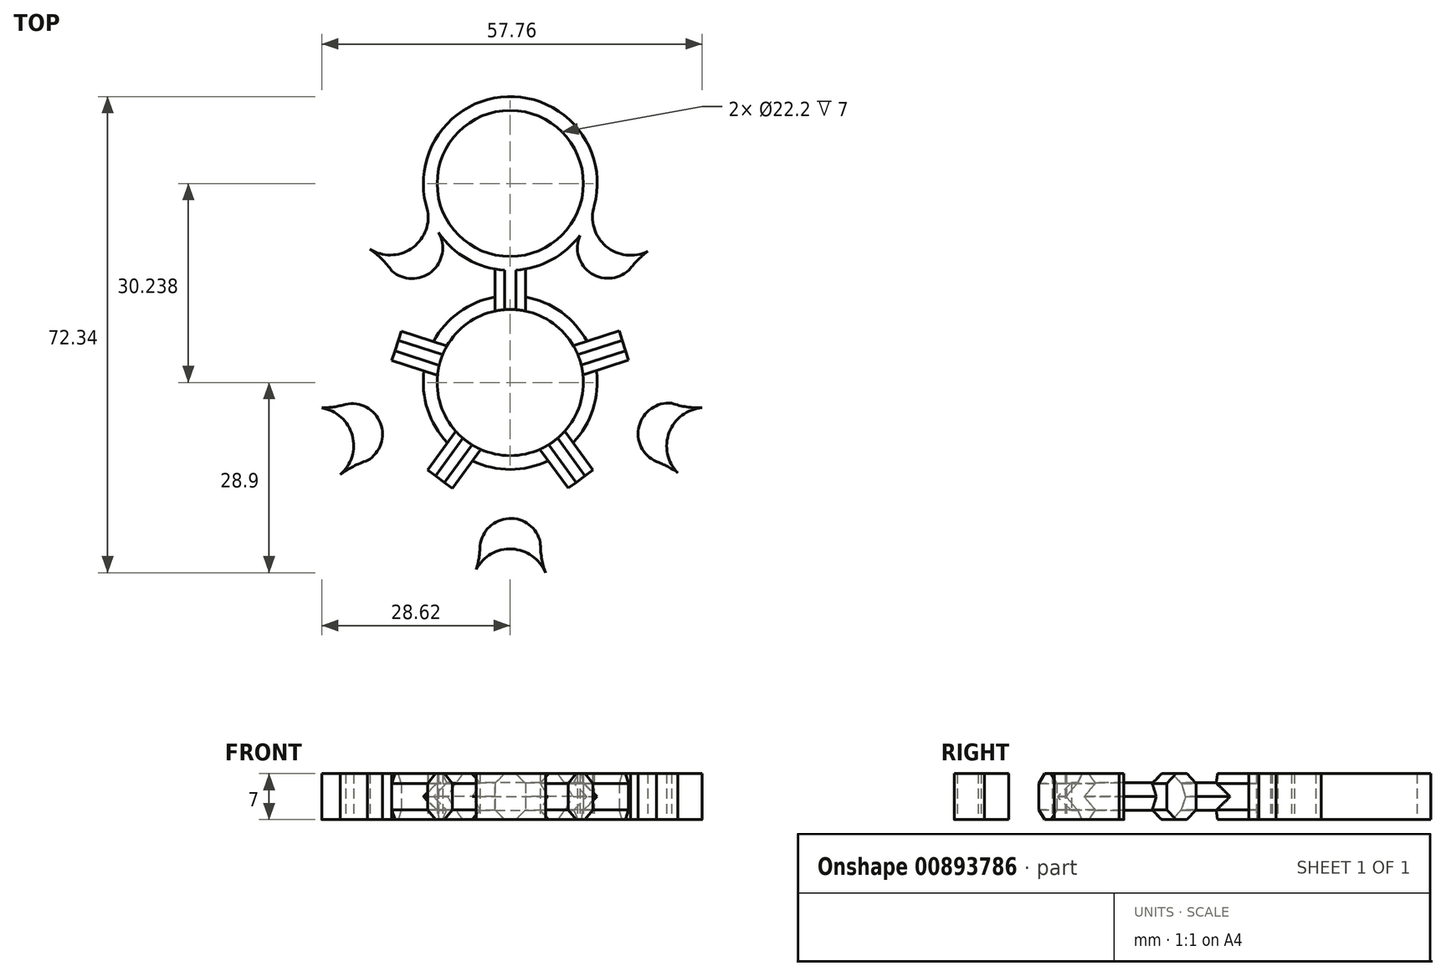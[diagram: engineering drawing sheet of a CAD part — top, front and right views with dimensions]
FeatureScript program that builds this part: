
annotation { "Feature Type Name" : "Feature", "Feature Type Description" : "" }
export const myFeature = defineFeature(function(context is Context, id is Id, definition is map)
    precondition{}
    {
        {
            var Q0;
            Q0=qCreatedBy(makeId("Top.planeOp"),FACE);
            var sketch = newSketch(context, id + "F0", { "sketchPlane" : qUnion([Q0])});
            skCircle(sketch, "E0", {"center": v(0, 0) * mm, "radius": 11.1 * mm});
            skCircle(sketch, "E1", {"center": v(0, 0) * mm, "radius": 13.2 * mm});
            skLineSegment(sketch, "E2", {"start": v(-2.34, 13) * mm, "end": v(-2.34, 18.14) * mm});
            skLineSegment(sketch, "E3", {"start": v(-2.34, 18.14) * mm, "end": v(2.33, 18.14) * mm});
            skLineSegment(sketch, "E4", {"start": v(2.33, 18.14) * mm, "end": v(2.33, 13) * mm});
            skCircle(sketch, "E5", {"center": v(0, 30.24) * mm, "radius": 13.2 * mm});
            skCircle(sketch, "E6", {"center": v(0, 30.24) * mm, "radius": 11.1 * mm});
            skCircle(sketch, "E7.1.0", {"center": v(-28.76, 9.34) * mm, "radius": 13.2 * mm});
            skCircle(sketch, "E7.1.1", {"center": v(-28.76, 9.34) * mm, "radius": 11.1 * mm});
            skLineSegment(sketch, "E7.1.2", {"start": v(-16.53, 7.82) * mm, "end": v(-11.64, 6.23) * mm});
            skLineSegment(sketch, "E7.1.3", {"start": v(-13.08, 1.78) * mm, "end": v(-17.98, 3.38) * mm});
            skLineSegment(sketch, "E7.1.4", {"start": v(-17.98, 3.38) * mm, "end": v(-16.53, 7.82) * mm});
            skCircle(sketch, "E7.2.0", {"center": v(-17.77, -24.46) * mm, "radius": 13.2 * mm});
            skCircle(sketch, "E7.2.1", {"center": v(-17.77, -24.46) * mm, "radius": 11.1 * mm});
            skLineSegment(sketch, "E7.2.2", {"start": v(-12.55, -13.3) * mm, "end": v(-9.52, -9.14) * mm});
            skLineSegment(sketch, "E7.2.3", {"start": v(-5.74, -11.89) * mm, "end": v(-8.77, -16.05) * mm});
            skLineSegment(sketch, "E7.2.4", {"start": v(-8.77, -16.05) * mm, "end": v(-12.55, -13.3) * mm});
            skCircle(sketch, "E7.3.0", {"center": v(17.77, -24.46) * mm, "radius": 13.2 * mm});
            skCircle(sketch, "E7.3.1", {"center": v(17.77, -24.46) * mm, "radius": 11.1 * mm});
            skLineSegment(sketch, "E7.3.2", {"start": v(8.78, -16.05) * mm, "end": v(5.75, -11.88) * mm});
            skLineSegment(sketch, "E7.3.3", {"start": v(9.53, -9.13) * mm, "end": v(12.56, -13.3) * mm});
            skLineSegment(sketch, "E7.3.4", {"start": v(12.56, -13.3) * mm, "end": v(8.78, -16.05) * mm});
            skCircle(sketch, "E7.4.0", {"center": v(28.76, 9.34) * mm, "radius": 13.2 * mm});
            skCircle(sketch, "E7.4.1", {"center": v(28.76, 9.34) * mm, "radius": 11.1 * mm});
            skLineSegment(sketch, "E7.4.2", {"start": v(17.97, 3.39) * mm, "end": v(13.08, 1.8) * mm});
            skLineSegment(sketch, "E7.4.3", {"start": v(11.63, 6.24) * mm, "end": v(16.53, 7.83) * mm});
            skLineSegment(sketch, "E7.4.4", {"start": v(16.53, 7.83) * mm, "end": v(17.97, 3.39) * mm});
            skArc(sketch, "E8", {"start": v(-17.98, 16.96) * mm, "mid": v(-11.96, 16.83) * mm, "end": v(-10.87, 22.75) * mm});
            skArc(sketch, "E9", {"start": v(-21.6, 20.43) * mm, "mid": v(-15.2, 20.23) * mm, "end": v(-12.5, 26.02) * mm});
            skArc(sketch, "E10.1.0", {"start": v(-26.1, -14.22) * mm, "mid": v(-23.93, -8.2) * mm, "end": v(-28.62, -3.86) * mm});
            skArc(sketch, "E10.1.1", {"start": v(-21.68, -11.86) * mm, "mid": v(-19.7, -6.17) * mm, "end": v(-25, -3.3) * mm});
            skArc(sketch, "E10.2.0", {"start": v(5.46, -29.22) * mm, "mid": v(0.41, -25.3) * mm, "end": v(-5.18, -28.4) * mm});
            skArc(sketch, "E10.2.1", {"start": v(4.57, -24.29) * mm, "mid": v(-0.22, -20.65) * mm, "end": v(-4.58, -24.8) * mm});
            skArc(sketch, "E10.3.0", {"start": v(29.48, -3.84) * mm, "mid": v(24.19, -7.43) * mm, "end": v(25.42, -13.7) * mm});
            skArc(sketch, "E10.3.1", {"start": v(24.51, -3.15) * mm, "mid": v(19.57, -6.59) * mm, "end": v(22.17, -12.02) * mm});
            skArc(sketch, "E10.4.0", {"start": v(12.76, 26.85) * mm, "mid": v(14.54, 20.7) * mm, "end": v(20.88, 19.94) * mm});
            skArc(sketch, "E10.4.1", {"start": v(10.57, 22.34) * mm, "mid": v(12.31, 16.58) * mm, "end": v(18.28, 17.37) * mm});
            skSolve(sketch);
        }
        {
            var Q0;
            {var subQ0=sQuery(id+"F0.wireOp",EDGE,"E8");Q0=makeQuery(id+"F0.imprint","IMPRINT",FACE,{"disambiguationData":[TD([[makeQuery(id+"F0.imprint","IMPRINT",EDGE,{"derivedFrom":subQ0}),1.0]])]});}
            var Q1;
            Q1=makeQuery(id+"F0.imprint","IMPRINT",FACE,{"disambiguationData":[TD([[makeQuery(id+"F0.imprint","IMPRINT",EDGE,{"derivedFrom":sQuery(id+"F0.wireOp",EDGE,"E7.1.1")}),-1.0]])]});
            var Q2;
            {var subQ5=sQuery(id+"F0.wireOp",EDGE,"E7.1.4");Q2=makeQuery(id+"F0.imprint","IMPRINT",FACE,{"disambiguationData":[TD([[makeQuery(id+"F0.imprint","IMPRINT",EDGE,{"derivedFrom":subQ5}),-1.0]])]});}
            var Q3;
            {var subQ0=sQuery(id+"F0.wireOp",EDGE,"E7.1.2");var subQ1=sQuery(id+"F0.wireOp",EDGE,"E1");var subQ2=makeQuery(id+"F0.imprint","INTERSECT",VERTEX,{"derivedFrom":[subQ1,subQ0]});Q3=makeQuery(id+"F0.imprint","IMPRINT",FACE,{"disambiguationData":[TD([[makeQuery(id+"F0.imprint","IMPRINT",EDGE,{"disambiguationData":[TD([[subQ2,-1.0]])],"derivedFrom":subQ1}),-1.0]])]});}
            var Q4;
            {var subQ0=sQuery(id+"F0.wireOp",EDGE,"E3");Q4=makeQuery(id+"F0.imprint","IMPRINT",FACE,{"disambiguationData":[TD([[makeQuery(id+"F0.imprint","IMPRINT",EDGE,{"derivedFrom":subQ0}),-1.0]])]});}
            var Q5;
            {var subQ4=sQuery(id+"F0.wireOp",EDGE,"E3");Q5=makeQuery(id+"F0.imprint","IMPRINT",FACE,{"disambiguationData":[TD([[makeQuery(id+"F0.imprint","IMPRINT",EDGE,{"derivedFrom":subQ4}),1.0]])]});}
            var Q6;
            {var subQ0=sQuery(id+"F0.wireOp",EDGE,"E10.4.1");Q6=makeQuery(id+"F0.imprint","IMPRINT",FACE,{"disambiguationData":[TD([[makeQuery(id+"F0.imprint","IMPRINT",EDGE,{"derivedFrom":subQ0}),1.0]])]});}
            var Q7;
            {var subQ5=sQuery(id+"F0.wireOp",EDGE,"E7.4.4");Q7=makeQuery(id+"F0.imprint","IMPRINT",FACE,{"disambiguationData":[TD([[makeQuery(id+"F0.imprint","IMPRINT",EDGE,{"derivedFrom":subQ5}),-1.0]])]});}
            var Q8;
            {var subQ5=sQuery(id+"F0.wireOp",EDGE,"E7.3.4");Q8=makeQuery(id+"F0.imprint","IMPRINT",FACE,{"disambiguationData":[TD([[makeQuery(id+"F0.imprint","IMPRINT",EDGE,{"derivedFrom":subQ5}),-1.0]])]});}
            var Q9;
            {var subQ5=sQuery(id+"F0.wireOp",EDGE,"E7.2.4");Q9=makeQuery(id+"F0.imprint","IMPRINT",FACE,{"disambiguationData":[TD([[makeQuery(id+"F0.imprint","IMPRINT",EDGE,{"derivedFrom":subQ5}),-1.0]])]});}
            var Q10;
            {var subQ0=sQuery(id+"F0.wireOp",EDGE,"E7.2.2");var subQ1=sQuery(id+"F0.wireOp",EDGE,"E1");var subQ2=makeQuery(id+"F0.imprint","INTERSECT",VERTEX,{"derivedFrom":[subQ1,subQ0]});Q10=makeQuery(id+"F0.imprint","IMPRINT",FACE,{"disambiguationData":[TD([[makeQuery(id+"F0.imprint","IMPRINT",EDGE,{"disambiguationData":[TD([[subQ2,-1.0]])],"derivedFrom":subQ1}),-1.0]])]});}
            var Q11;
            Q11=makeQuery(id+"F0.imprint","IMPRINT",FACE,{"disambiguationData":[TD([[makeQuery(id+"F0.imprint","IMPRINT",EDGE,{"derivedFrom":sQuery(id+"F0.wireOp",EDGE,"E0")}),-1.0]])]});
            var Q12;
            {var subQ0=sQuery(id+"F0.wireOp",EDGE,"E7.4.2");var subQ1=sQuery(id+"F0.wireOp",EDGE,"E1");var subQ2=makeQuery(id+"F0.imprint","INTERSECT",VERTEX,{"derivedFrom":[subQ1,subQ0]});Q12=makeQuery(id+"F0.imprint","IMPRINT",FACE,{"disambiguationData":[TD([[makeQuery(id+"F0.imprint","IMPRINT",EDGE,{"disambiguationData":[TD([[subQ2,-1.0]])],"derivedFrom":subQ1}),-1.0]])]});}
            var Q13;
            {var subQ0=sQuery(id+"F0.wireOp",EDGE,"E2");var subQ1=sQuery(id+"F0.wireOp",EDGE,"E1");var subQ2=makeQuery(id+"F0.imprint","INTERSECT",VERTEX,{"derivedFrom":[subQ1,subQ0]});Q13=makeQuery(id+"F0.imprint","IMPRINT",FACE,{"disambiguationData":[TD([[makeQuery(id+"F0.imprint","IMPRINT",EDGE,{"disambiguationData":[TD([[subQ2,1.0]])],"derivedFrom":subQ1}),-1.0]])]});}
            var Q14;
            {var subQ0=sQuery(id+"F0.wireOp",EDGE,"E7.3.2");var subQ1=sQuery(id+"F0.wireOp",EDGE,"E1");var subQ2=makeQuery(id+"F0.imprint","INTERSECT",VERTEX,{"derivedFrom":[subQ1,subQ0]});Q14=makeQuery(id+"F0.imprint","IMPRINT",FACE,{"disambiguationData":[TD([[makeQuery(id+"F0.imprint","IMPRINT",EDGE,{"disambiguationData":[TD([[subQ2,-1.0]])],"derivedFrom":subQ1}),-1.0]])]});}
            var Q15;
            Q15=makeQuery(id+"F0.imprint","IMPRINT",FACE,{"disambiguationData":[TD([[makeQuery(id+"F0.imprint","IMPRINT",EDGE,{"derivedFrom":sQuery(id+"F0.wireOp",EDGE,"E7.3.1")}),-1.0]])]});
            var Q16;
            {var subQ3=sQuery(id+"F0.wireOp",EDGE,"E10.2.1");Q16=makeQuery(id+"F0.imprint","IMPRINT",FACE,{"disambiguationData":[TD([[makeQuery(id+"F0.imprint","IMPRINT",EDGE,{"derivedFrom":subQ3}),1.0]])]});}
            var Q17;
            Q17=makeQuery(id+"F0.imprint","IMPRINT",FACE,{"disambiguationData":[TD([[makeQuery(id+"F0.imprint","IMPRINT",EDGE,{"derivedFrom":sQuery(id+"F0.wireOp",EDGE,"E7.2.1")}),-1.0]])]});
            var Q18;
            {var subQ3=sQuery(id+"F0.wireOp",EDGE,"E10.1.1");Q18=makeQuery(id+"F0.imprint","IMPRINT",FACE,{"disambiguationData":[TD([[makeQuery(id+"F0.imprint","IMPRINT",EDGE,{"derivedFrom":subQ3}),1.0]])]});}
            var Q19;
            Q19=makeQuery(id+"F0.imprint","IMPRINT",FACE,{"disambiguationData":[TD([[makeQuery(id+"F0.imprint","IMPRINT",EDGE,{"derivedFrom":sQuery(id+"F0.wireOp",EDGE,"E7.4.1")}),-1.0]])]});
            var Q20;
            {var subQ3=sQuery(id+"F0.wireOp",EDGE,"E10.3.1");Q20=makeQuery(id+"F0.imprint","IMPRINT",FACE,{"disambiguationData":[TD([[makeQuery(id+"F0.imprint","IMPRINT",EDGE,{"derivedFrom":subQ3}),1.0]])]});}
            extrude(context, id + "F1", {"entities" : qUnion([Q0, Q1, Q2, Q3, Q4, Q5, Q6, Q7, Q8, Q9, Q10, Q11, Q12, Q13, Q14, Q15, Q16, Q17, Q18, Q19, Q20]), "depth" : 7 * mm, "offsetDistance" : 25 * mm});
        }
        {
            var Q0;
            {var subQ0=sQuery(id+"F0.wireOp",EDGE,"E1");Q0=makeQuery(id+"F1.opExtrude","CAP_EDGE",EDGE,{"disambiguationData":[OSD([subQ0]),TDD([makeQuery(id+"F0.imprint","IMPRINT",EDGE,{"disambiguationData":[TD([[makeQuery(id+"F0.imprint","INTERSECT",VERTEX,{"derivedFrom":[subQ0,sQuery(id+"F0.wireOp",EDGE,"E7.3.3")]}),-1.0]])],"derivedFrom":subQ0})])],"isStart":false});}
            var Q1;
            {var subQ0=sQuery(id+"F0.wireOp",EDGE,"E1");Q1=makeQuery(id+"F1.opExtrude","CAP_EDGE",EDGE,{"disambiguationData":[OSD([subQ0]),TDD([makeQuery(id+"F0.imprint","IMPRINT",EDGE,{"disambiguationData":[TD([[makeQuery(id+"F0.imprint","INTERSECT",VERTEX,{"derivedFrom":[subQ0,sQuery(id+"F0.wireOp",EDGE,"E4")]}),1.0]])],"derivedFrom":subQ0})])],"isStart":false});}
            var Q2;
            {var subQ0=sQuery(id+"F0.wireOp",EDGE,"E1");Q2=makeQuery(id+"F1.opExtrude","CAP_EDGE",EDGE,{"disambiguationData":[OSD([subQ0]),TDD([makeQuery(id+"F0.imprint","IMPRINT",EDGE,{"disambiguationData":[TD([[makeQuery(id+"F0.imprint","INTERSECT",VERTEX,{"derivedFrom":[subQ0,sQuery(id+"F0.wireOp",EDGE,"E2")]}),-1.0]])],"derivedFrom":subQ0})])],"isStart":false});}
            var Q3;
            {var subQ0=sQuery(id+"F0.wireOp",EDGE,"E1");Q3=makeQuery(id+"F1.opExtrude","CAP_EDGE",EDGE,{"disambiguationData":[OSD([subQ0]),TDD([makeQuery(id+"F0.imprint","IMPRINT",EDGE,{"disambiguationData":[TD([[makeQuery(id+"F0.imprint","INTERSECT",VERTEX,{"derivedFrom":[subQ0,sQuery(id+"F0.wireOp",EDGE,"E7.1.3")]}),-1.0]])],"derivedFrom":subQ0})])],"isStart":false});}
            var Q4;
            {var subQ0=sQuery(id+"F0.wireOp",EDGE,"E1");Q4=makeQuery(id+"F1.opExtrude","CAP_EDGE",EDGE,{"disambiguationData":[OSD([subQ0]),TDD([makeQuery(id+"F0.imprint","IMPRINT",EDGE,{"disambiguationData":[TD([[makeQuery(id+"F0.imprint","INTERSECT",VERTEX,{"derivedFrom":[subQ0,sQuery(id+"F0.wireOp",EDGE,"E7.2.3")]}),-1.0]])],"derivedFrom":subQ0})])],"isStart":false});}
            chamfer(context, id + "F2", {"entities" : qUnion([Q0, Q1, Q2, Q3, Q4]), "width" : 3.5 * mm, "tangentPropagation" : true});
        }
        {
            var Q0;
            {var subQ0=sQuery(id+"F0.wireOp",EDGE,"E1");Q0=makeQuery(id+"F1.opExtrude","CAP_EDGE",EDGE,{"disambiguationData":[OSD([subQ0]),TDD([makeQuery(id+"F0.imprint","IMPRINT",EDGE,{"disambiguationData":[TD([[makeQuery(id+"F0.imprint","INTERSECT",VERTEX,{"derivedFrom":[subQ0,sQuery(id+"F0.wireOp",EDGE,"E4")]}),1.0]])],"derivedFrom":subQ0})])],"isStart":true});}
            var Q1;
            {var subQ0=sQuery(id+"F0.wireOp",EDGE,"E1");Q1=makeQuery(id+"F1.opExtrude","CAP_EDGE",EDGE,{"disambiguationData":[OSD([subQ0]),TDD([makeQuery(id+"F0.imprint","IMPRINT",EDGE,{"disambiguationData":[TD([[makeQuery(id+"F0.imprint","INTERSECT",VERTEX,{"derivedFrom":[subQ0,sQuery(id+"F0.wireOp",EDGE,"E2")]}),-1.0]])],"derivedFrom":subQ0})])],"isStart":true});}
            var Q2;
            {var subQ0=sQuery(id+"F0.wireOp",EDGE,"E1");Q2=makeQuery(id+"F1.opExtrude","CAP_EDGE",EDGE,{"disambiguationData":[OSD([subQ0]),TDD([makeQuery(id+"F0.imprint","IMPRINT",EDGE,{"disambiguationData":[TD([[makeQuery(id+"F0.imprint","INTERSECT",VERTEX,{"derivedFrom":[subQ0,sQuery(id+"F0.wireOp",EDGE,"E7.1.3")]}),-1.0]])],"derivedFrom":subQ0})])],"isStart":true});}
            var Q3;
            {var subQ0=sQuery(id+"F0.wireOp",EDGE,"E1");Q3=makeQuery(id+"F1.opExtrude","CAP_EDGE",EDGE,{"disambiguationData":[OSD([subQ0]),TDD([makeQuery(id+"F0.imprint","IMPRINT",EDGE,{"disambiguationData":[TD([[makeQuery(id+"F0.imprint","INTERSECT",VERTEX,{"derivedFrom":[subQ0,sQuery(id+"F0.wireOp",EDGE,"E7.2.3")]}),-1.0]])],"derivedFrom":subQ0})])],"isStart":true});}
            var Q4;
            {var subQ0=sQuery(id+"F0.wireOp",EDGE,"E1");Q4=makeQuery(id+"F1.opExtrude","CAP_EDGE",EDGE,{"disambiguationData":[OSD([subQ0]),TDD([makeQuery(id+"F0.imprint","IMPRINT",EDGE,{"disambiguationData":[TD([[makeQuery(id+"F0.imprint","INTERSECT",VERTEX,{"derivedFrom":[subQ0,sQuery(id+"F0.wireOp",EDGE,"E7.3.3")]}),-1.0]])],"derivedFrom":subQ0})])],"isStart":true});}
            chamfer(context, id + "F3", {"entities" : qUnion([Q0, Q1, Q2, Q3, Q4]), "width" : 3.5 * mm, "tangentPropagation" : true});
        }
        {
            var Q0;
            Q0=makeQuery(id+"F1.opExtrude","CAP_EDGE",EDGE,{"disambiguationData":[OSD([sQuery(id+"F0.wireOp",EDGE,"E10.3.0")])],"isStart":true});
            var Q1;
            Q1=makeQuery(id+"F1.opExtrude","CAP_EDGE",EDGE,{"disambiguationData":[OSD([sQuery(id+"F0.wireOp",EDGE,"E10.4.0")])],"isStart":true});
            var Q2;
            Q2=makeQuery(id+"F1.opExtrude","CAP_EDGE",EDGE,{"disambiguationData":[OSD([sQuery(id+"F0.wireOp",EDGE,"E9")])],"isStart":true});
            var Q3;
            Q3=makeQuery(id+"F1.opExtrude","CAP_EDGE",EDGE,{"disambiguationData":[OSD([sQuery(id+"F0.wireOp",EDGE,"E10.1.0")])],"isStart":true});
            var Q4;
            Q4=makeQuery(id+"F1.opExtrude","CAP_EDGE",EDGE,{"disambiguationData":[OSD([sQuery(id+"F0.wireOp",EDGE,"E10.2.0")])],"isStart":true});
            fillet(context, id + "F4", {"entities" : qUnion([Q0, Q1, Q2, Q3, Q4]), "radius" : 0.02 * mm, "tangentPropagation" : true, "allowEdgeOverflow" : false});
        }
        {
            var Q0;
            Q0=makeQuery(id+"F1.opExtrude","CAP_EDGE",EDGE,{"disambiguationData":[OSD([sQuery(id+"F0.wireOp",EDGE,"E4")])],"isStart":true});
            var Q1;
            Q1=makeQuery(id+"F1.opExtrude","CAP_EDGE",EDGE,{"disambiguationData":[OSD([sQuery(id+"F0.wireOp",EDGE,"E2")])],"isStart":true});
            var Q2;
            Q2=makeQuery(id+"F1.opExtrude","CAP_EDGE",EDGE,{"disambiguationData":[OSD([sQuery(id+"F0.wireOp",EDGE,"E7.1.2")])],"isStart":true});
            var Q3;
            Q3=makeQuery(id+"F1.opExtrude","CAP_EDGE",EDGE,{"disambiguationData":[OSD([sQuery(id+"F0.wireOp",EDGE,"E7.1.3")])],"isStart":true});
            var Q4;
            Q4=makeQuery(id+"F1.opExtrude","CAP_EDGE",EDGE,{"disambiguationData":[OSD([sQuery(id+"F0.wireOp",EDGE,"E7.2.2")])],"isStart":true});
            var Q5;
            Q5=makeQuery(id+"F1.opExtrude","CAP_EDGE",EDGE,{"disambiguationData":[OSD([sQuery(id+"F0.wireOp",EDGE,"E7.2.3")])],"isStart":true});
            var Q6;
            Q6=makeQuery(id+"F1.opExtrude","CAP_EDGE",EDGE,{"disambiguationData":[OSD([sQuery(id+"F0.wireOp",EDGE,"E7.3.2")])],"isStart":true});
            var Q7;
            Q7=makeQuery(id+"F1.opExtrude","CAP_EDGE",EDGE,{"disambiguationData":[OSD([sQuery(id+"F0.wireOp",EDGE,"E7.3.3")])],"isStart":true});
            var Q8;
            Q8=makeQuery(id+"F1.opExtrude","CAP_EDGE",EDGE,{"disambiguationData":[OSD([sQuery(id+"F0.wireOp",EDGE,"E7.4.2")])],"isStart":true});
            var Q9;
            Q9=makeQuery(id+"F1.opExtrude","CAP_EDGE",EDGE,{"disambiguationData":[OSD([sQuery(id+"F0.wireOp",EDGE,"E7.4.3")])],"isStart":true});
            chamfer(context, id + "F5", {"entities" : qUnion([Q0, Q1, Q2, Q3, Q4, Q5, Q6, Q7, Q8, Q9]), "width" : 1.5 * mm, "tangentPropagation" : true});
        }
        {
            var Q0;
            Q0=makeQuery(id+"F1.opExtrude","CAP_EDGE",EDGE,{"disambiguationData":[OSD([sQuery(id+"F0.wireOp",EDGE,"E7.1.2")])],"isStart":false});
            var Q1;
            Q1=makeQuery(id+"F1.opExtrude","CAP_EDGE",EDGE,{"disambiguationData":[OSD([sQuery(id+"F0.wireOp",EDGE,"E7.1.3")])],"isStart":false});
            var Q2;
            Q2=makeQuery(id+"F1.opExtrude","CAP_EDGE",EDGE,{"disambiguationData":[OSD([sQuery(id+"F0.wireOp",EDGE,"E2")])],"isStart":false});
            var Q3;
            Q3=makeQuery(id+"F1.opExtrude","CAP_EDGE",EDGE,{"disambiguationData":[OSD([sQuery(id+"F0.wireOp",EDGE,"E4")])],"isStart":false});
            var Q4;
            Q4=makeQuery(id+"F1.opExtrude","CAP_EDGE",EDGE,{"disambiguationData":[OSD([sQuery(id+"F0.wireOp",EDGE,"E7.4.3")])],"isStart":false});
            var Q5;
            Q5=makeQuery(id+"F1.opExtrude","CAP_EDGE",EDGE,{"disambiguationData":[OSD([sQuery(id+"F0.wireOp",EDGE,"E7.4.2")])],"isStart":false});
            var Q6;
            Q6=makeQuery(id+"F1.opExtrude","CAP_EDGE",EDGE,{"disambiguationData":[OSD([sQuery(id+"F0.wireOp",EDGE,"E7.3.3")])],"isStart":false});
            var Q7;
            Q7=makeQuery(id+"F1.opExtrude","CAP_EDGE",EDGE,{"disambiguationData":[OSD([sQuery(id+"F0.wireOp",EDGE,"E7.3.2")])],"isStart":false});
            var Q8;
            Q8=makeQuery(id+"F1.opExtrude","CAP_EDGE",EDGE,{"disambiguationData":[OSD([sQuery(id+"F0.wireOp",EDGE,"E7.2.3")])],"isStart":false});
            var Q9;
            Q9=makeQuery(id+"F1.opExtrude","CAP_EDGE",EDGE,{"disambiguationData":[OSD([sQuery(id+"F0.wireOp",EDGE,"E7.2.2")])],"isStart":false});
            chamfer(context, id + "F6", {"entities" : qUnion([Q0, Q1, Q2, Q3, Q4, Q5, Q6, Q7, Q8, Q9]), "width" : 1.5 * mm, "tangentPropagation" : true});
        }
        {
            var Q0;
            Q0=qCreatedBy(makeId("Front.planeOp"),FACE);
            cPlane(context, id + "F7", {"entities" : qUnion([Q0]), "cplaneType" : CPlaneType.OFFSET, "offset" : 41.3 * mm, "width" : 150 * mm, "height" : 150 * mm});
        }
        {
            var Q0;
            Q0=qCreatedBy(id+"F7.planeOp",FACE);
            var sketch = newSketch(context, id + "F8", { "sketchPlane" : qUnion([Q0])});
            skText(sketch, "E11", { "text": "EJJ", "fontName": "AllertaStencil-Regular.ttf"});
            const initialGuessF8  = {"E11": [-0.02576, 0.00048, 1, 0, 0.006]};
            skSetInitialGuess(sketch, initialGuessF8);
            skSolve(sketch);
        }
        {
            var Q0;
            Q0 = qSketchRegion(id + "F8", true);
            extrude(context, id + "F9", {"entities" : qUnion([Q0]), "operationType" : NewBodyOperationType.REMOVE, "oppositeDirection" : true, "depth" : 16.8 * mm, "offsetDistance" : 25 * mm});
        }
    });
